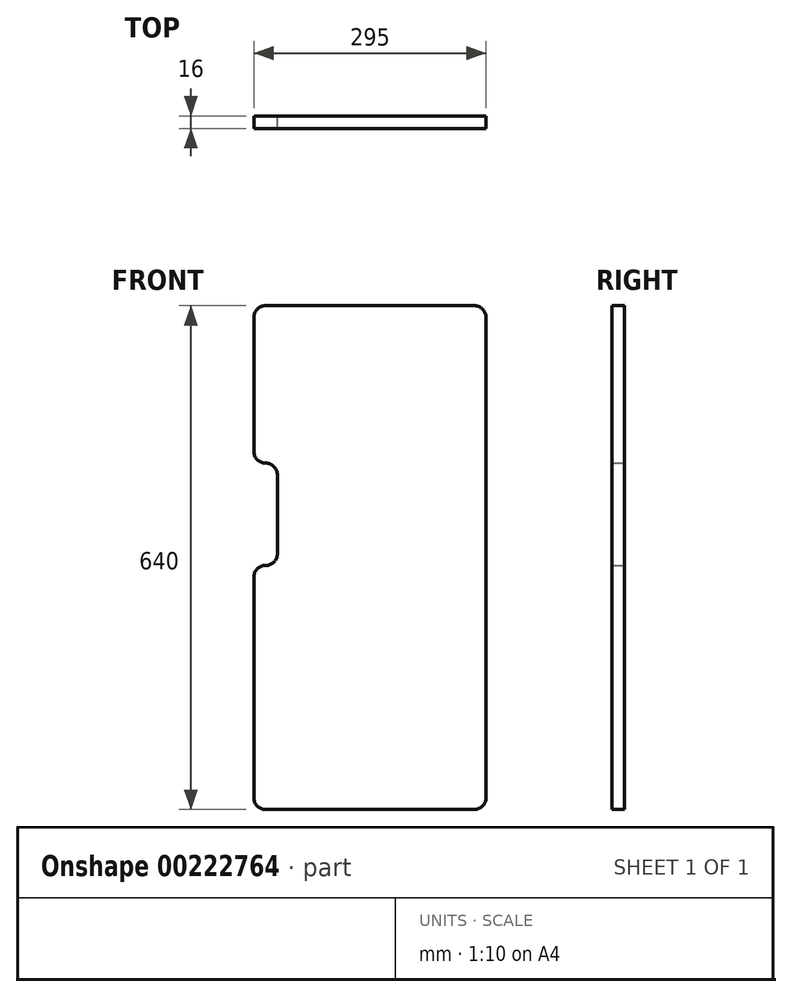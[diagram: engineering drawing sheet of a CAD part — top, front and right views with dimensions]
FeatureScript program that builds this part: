
annotation { "Feature Type Name" : "Feature", "Feature Type Description" : "" }
export const myFeature = defineFeature(function(context is Context, id is Id, definition is map)
    precondition{}
    {
        {
            var Q0;
            Q0=qCreatedBy(makeId("Front.planeOp"),FACE);
            var sketch = newSketch(context, id + "F0", { "sketchPlane" : qUnion([Q0])});
            skLineSegment(sketch, "E0.bottom", {"start": v(15, 640) * mm, "end": v(280, 640) * mm});
            skLineSegment(sketch, "E0.top", {"start": v(15, 0) * mm, "end": v(280, 0) * mm});
            skLineSegment(sketch, "E0.left", {"start": v(0, 625) * mm, "end": v(0, 15) * mm, "construction": true});
            skLineSegment(sketch, "E0.right", {"start": v(295, 625) * mm, "end": v(295, 15) * mm});
            skPoint(sketch, "E1.visualSharp", {"position": v(0, 640) * mm});
            skArc(sketch, "E1.filletArc", {"start": v(15, 640) * mm, "mid": v(4.4, 635.6) * mm, "end": v(0, 625) * mm});
            skPoint(sketch, "E2.visualSharp", {"position": v(295, 640) * mm});
            skArc(sketch, "E2.filletArc", {"start": v(295, 625) * mm, "mid": v(290.6, 635.6) * mm, "end": v(280, 640) * mm});
            skPoint(sketch, "E3.visualSharp", {"position": v(295, 0) * mm});
            skArc(sketch, "E3.filletArc", {"start": v(280, 0) * mm, "mid": v(290.6, 4.4) * mm, "end": v(295, 15) * mm});
            skPoint(sketch, "E4.visualSharp", {"position": v(0, 0) * mm});
            skArc(sketch, "E4.filletArc", {"start": v(0, 15) * mm, "mid": v(4.4, 4.4) * mm, "end": v(15, 0) * mm});
            skLineSegment(sketch, "E5.bottom", {"start": v(15, 440) * mm, "end": v(15, 440) * mm});
            skLineSegment(sketch, "E5.top", {"start": v(15, 310) * mm, "end": v(15, 310) * mm});
            skLineSegment(sketch, "E5.left", {"start": v(0, 440) * mm, "end": v(0, 310) * mm, "construction": true});
            skLineSegment(sketch, "E5.right", {"start": v(30, 425) * mm, "end": v(30, 325) * mm});
            skLineSegment(sketch, "E6", {"start": v(0, 15) * mm, "end": v(0, 310) * mm, "construction": true});
            skLineSegment(sketch, "E7", {"start": v(0, 440) * mm, "end": v(0, 625) * mm, "construction": true});
            skPoint(sketch, "E8.visualSharp", {"position": v(30, 440) * mm});
            skArc(sketch, "E8.filletArc", {"start": v(30, 425) * mm, "mid": v(25.6, 435.6) * mm, "end": v(15, 440) * mm});
            skPoint(sketch, "E9.visualSharp", {"position": v(30, 310) * mm});
            skArc(sketch, "E9.filletArc", {"start": v(15, 310) * mm, "mid": v(25.6, 314.4) * mm, "end": v(30, 325) * mm});
            skLineSegment(sketch, "E10", {"start": v(0, 625) * mm, "end": v(0, 455) * mm});
            skLineSegment(sketch, "E11", {"start": v(0, 15) * mm, "end": v(0, 295) * mm});
            skPoint(sketch, "E12.visualSharp", {"position": v(0, 440) * mm});
            skArc(sketch, "E12.filletArc", {"start": v(0, 455) * mm, "mid": v(4.4, 444.4) * mm, "end": v(15, 440) * mm});
            skPoint(sketch, "E13.visualSharp", {"position": v(0, 310) * mm});
            skArc(sketch, "E13.filletArc", {"start": v(15, 310) * mm, "mid": v(4.4, 305.6) * mm, "end": v(0, 295) * mm});
            skSolve(sketch);
        }
        {
            var Q0;
            Q0=makeQuery(id+"F0.imprint","IMPRINT",FACE,{"disambiguationData":[TD([[makeQuery(id+"F0.imprint","IMPRINT",EDGE,{"derivedFrom":sQuery(id+"F0.wireOp",EDGE,"E0.bottom")}),-1.0]])]});
            extrude(context, id + "F1", {"entities" : qUnion([Q0]), "depth" : 16 * mm});
        }
    });
